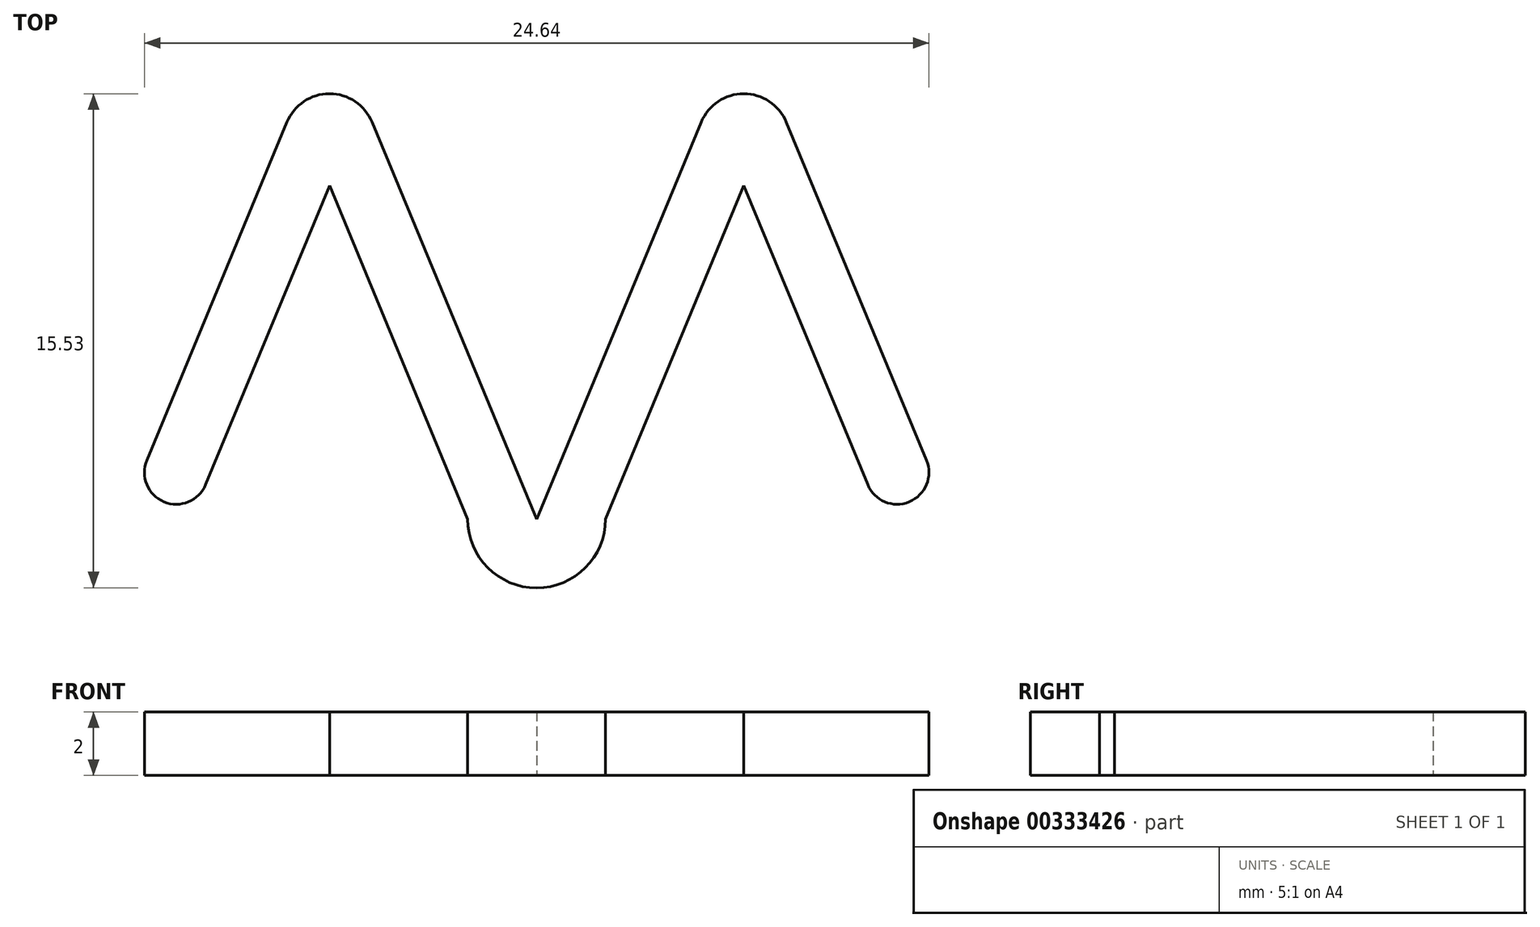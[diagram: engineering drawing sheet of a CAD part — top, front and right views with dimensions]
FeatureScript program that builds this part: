
annotation { "Feature Type Name" : "Feature", "Feature Type Description" : "" }
export const myFeature = defineFeature(function(context is Context, id is Id, definition is map)
    precondition{}
    {
        {
            var Q0;
            Q0=qCreatedBy(makeId("Top.planeOp"),FACE);
            var sketch = newSketch(context, id + "F0", { "sketchPlane" : qUnion([Q0])});
            skLineSegment(sketch, "E0", {"start": v(0, 0) * mm, "end": v(6.5, 15.7) * mm});
            skLineSegment(sketch, "E1", {"start": v(6.5, 15.7) * mm, "end": v(12.63, 0.92) * mm});
            skLineSegment(sketch, "E2", {"start": v(12.63, 0.92) * mm, "end": v(10.78, 0.16) * mm});
            skLineSegment(sketch, "E3", {"start": v(10.78, 0.16) * mm, "end": v(6.5, 10.48) * mm});
            skLineSegment(sketch, "E4", {"start": v(6.5, 10.48) * mm, "end": v(2.16, 0) * mm});
            skLineSegment(sketch, "E5.MirrorCS", {"start": v(-6.5, 10.48) * mm, "end": v(-2.16, 0) * mm});
            skPoint(sketch, "E6", {"position": v(-6.5, 12.48) * mm});
            skArc(sketch, "E7", {"start": v(-5.17, 12.48) * mm, "mid": v(-6.5, 13.37) * mm, "end": v(-7.84, 12.48) * mm});
            skPoint(sketch, "E8", {"position": v(6.5, 12.48) * mm});
            skArc(sketch, "E9", {"start": v(7.84, 12.48) * mm, "mid": v(6.5, 13.37) * mm, "end": v(5.17, 12.48) * mm});
            skPoint(sketch, "E10", {"position": v(-11.32, 1.47) * mm});
            skArc(sketch, "E11", {"start": v(-12.25, 1.85) * mm, "mid": v(-11.7, 0.54) * mm, "end": v(-10.4, 1.08) * mm});
            skArc(sketch, "E12.MirrorCS", {"start": v(12.25, 1.85) * mm, "mid": v(11.7, 0.54) * mm, "end": v(10.4, 1.08) * mm});
            skArc(sketch, "E13", {"start": v(-2.16, 0) * mm, "mid": v(0, -2.16) * mm, "end": v(2.16, 0) * mm});
            skLineSegment(sketch, "E14", {"start": v(-7.84, 12.48) * mm, "end": v(-12.25, 1.85) * mm});
            skLineSegment(sketch, "E15", {"start": v(-10.4, 1.08) * mm, "end": v(-6.5, 10.48) * mm});
            skLineSegment(sketch, "E16", {"start": v(-6.5, 11.93) * mm, "end": v(-11.32, 1.47) * mm});
            skLineSegment(sketch, "E17", {"start": v(-5.17, 12.48) * mm, "end": v(0, 0) * mm});
            skSolve(sketch);
        }
        {
            var Q0;
            {var subQ18=sQuery(id+"F0.wireOp",EDGE,"E4");Q0=makeQuery(id+"F0.imprint","IMPRINT",FACE,{"disambiguationData":[TD([[makeQuery(id+"F0.imprint","IMPRINT",EDGE,{"derivedFrom":subQ18}),-1.0]])]});}
            extrude(context, id + "F1", {"entities" : qUnion([Q0]), "depth" : 2 * mm});
        }
    });
